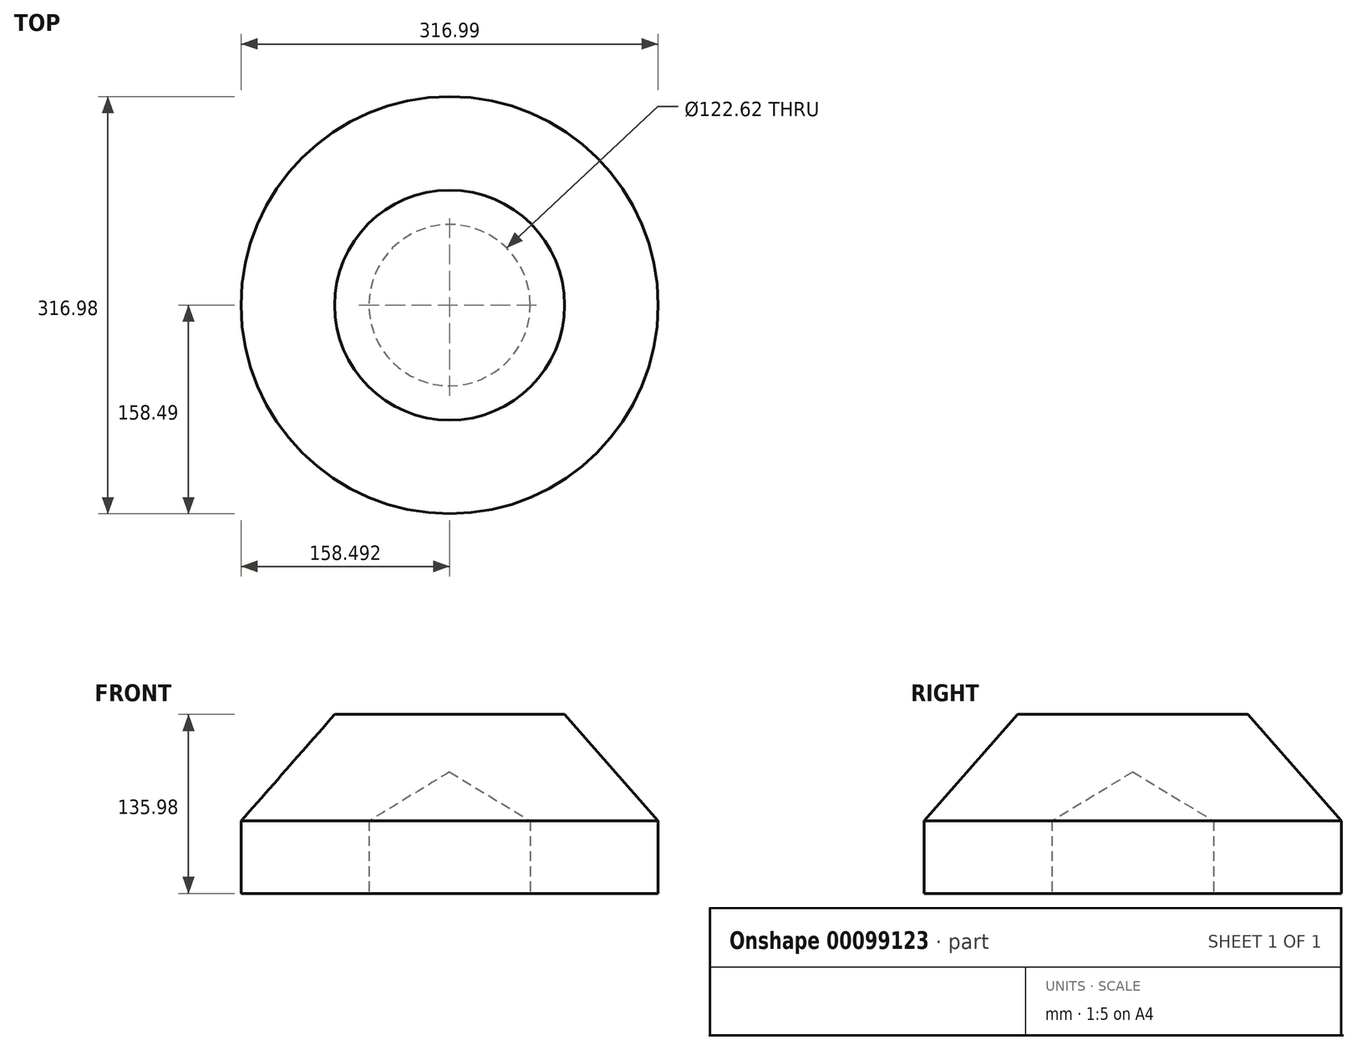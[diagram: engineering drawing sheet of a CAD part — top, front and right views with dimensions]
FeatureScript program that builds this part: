
annotation { "Feature Type Name" : "Feature", "Feature Type Description" : "" }
export const myFeature = defineFeature(function(context is Context, id is Id, definition is map)
    precondition{}
    {
        {
            var Q0;
            Q0=qCreatedBy(makeId("Front.planeOp"),FACE);
            var sketch = newSketch(context, id + "F0", { "sketchPlane" : qUnion([Q0])});
            skLineSegment(sketch, "E0.bottom", {"start": v(-48.6, 27.5) * mm, "end": v(48.6, 27.5) * mm});
            skLineSegment(sketch, "E0.top", {"start": v(-48.6, -27.5) * mm, "end": v(48.6, -27.5) * mm});
            skLineSegment(sketch, "E0.left", {"start": v(-48.6, 27.5) * mm, "end": v(-48.6, -27.5) * mm});
            skLineSegment(sketch, "E0.right", {"start": v(48.6, 27.5) * mm, "end": v(48.6, -27.5) * mm});
            skPoint(sketch, "E0.middle", {"position": v(0, 0) * mm});
            skLineSegment(sketch, "E1.bottom", {"start": v(109.9, 64.77) * mm, "end": v(22.5, 64.77) * mm});
            skLineSegment(sketch, "E1.top", {"start": v(109.9, 108.47) * mm, "end": v(22.5, 108.47) * mm});
            skLineSegment(sketch, "E1.left", {"start": v(109.9, 64.77) * mm, "end": v(109.9, 108.47) * mm});
            skLineSegment(sketch, "E1.right", {"start": v(22.5, 64.77) * mm, "end": v(22.5, 108.47) * mm});
            skPoint(sketch, "E1.middle", {"position": v(66.2, 86.62) * mm});
            skLineSegment(sketch, "E2", {"start": v(-48.6, 27.5) * mm, "end": v(22.5, 108.47) * mm});
            skLineSegment(sketch, "E3", {"start": v(109.9, 64.77) * mm, "end": v(48.6, 27.5) * mm});
            skSolve(sketch);
        }
        {
            var Q0;
            Q0 = qSketchRegion(id + "F0", true);
            var Q1;
            Q1=sQuery(id+"F0.wireOp",EDGE,"E1.left");
            revolve(context, id + "F1", {"entities" : qUnion([Q0]), "axis" : qUnion([Q1]), "revolveType" : RevolveType.FULL});
        }
    });
